# Revit family: ASL2
name_source: partatom
category: Lighting Fixtures
revit_build: Autodesk Revit 2017 (Build: 20160225_1515(x64)
units: mm (PartAtom-declared; Revit-internal decimal feet)

## family parameters
Always vertical = Yes
Cut with Voids When Loaded = No
Light Source = Yes
OmniClass Number = 23.80.70.14.21
OmniClass Title = Street and Roadway Lighting
Part Type = Normal
Room Calculation Point = No
Round Connector Dimension = Use Diameter
Shared = No
Work Plane-Based = No

## types (1)
- ASL2
    Apparent Load = 40 VA
    Assembly Code = D5020200
    Center Width = 3 "
    Certifications = Listed to UL1598 and CSA C22.2#250.0-24 for
wet locations and 40˚C ambient temperatures
• 1.5G rated for ANSI C136.31 high vibration
applications
• IP65 optical assembly
    Color Filter = 16777215
    Color Temperature = 0 K
    Depth = 18.44 "
    Description = Compact sleek design with multiple LED configurations and simple installation. The Airo includes a universal mounting block for easy pole installation or mast arm option for 2-3/8 ft OD roadway brackets.
    Dimming Lamp Color Temperature Shift = <None>
    Emit Shape Visible in Rendering = No
    Emit from Rectangle Length = 10 "
    Emit from Rectangle Width = 10 "
    Features = Compact sleek design with multiple LED configurations and
simple installation
• The Airo includes a universal mounting block for easy pole
installation or mast arm option for 2-3/8 ft OD roadway brackets
• Capable of replacing up to 1000w HID luminaires
• Micro Strike optical distributions of Type 2, 3, 4W or 5QW
• Tool-less entry option for easy installation and maintenance
• 1.5G rated for high vibration applications including bridges and
overpasses
    Finish = Powder Coat-Hubbell-Black
    Fixture Height = 7.5 "
    Lamp = default
    Lens = Glass-Hubbell-Temper Molded
    Manufacturer = Hubbell Lighting
    Model = ASL2
    Number of Poles = 1
    Offset From Pole = 6.12 "
    Photometric Notes = More IES files download on Photometric Web Link
    Photometric Web File = ASL2-320L-145-3K7-2.ies
    Photometric Web Link = https://www.hubbell.com
    Pole = Yes
    Pole Width = 4 "
    Power Factor = 1
    Product Documentation Link = https://hubbellcdn.com
    Product Page URL = https://www.hubbell.com
    Series = Airo Micro Strike
    Tilt Angle = 90.00°
    Type Comments = Lighting Fixture
    URL = https://www.hubbell.com
    Voltage = 0 V
    Wattage Comments = 40
    Width = 14 "

## geometry (parser evidence)
native form markers: Sweep x11
no freeform markers — native parametric forms only
